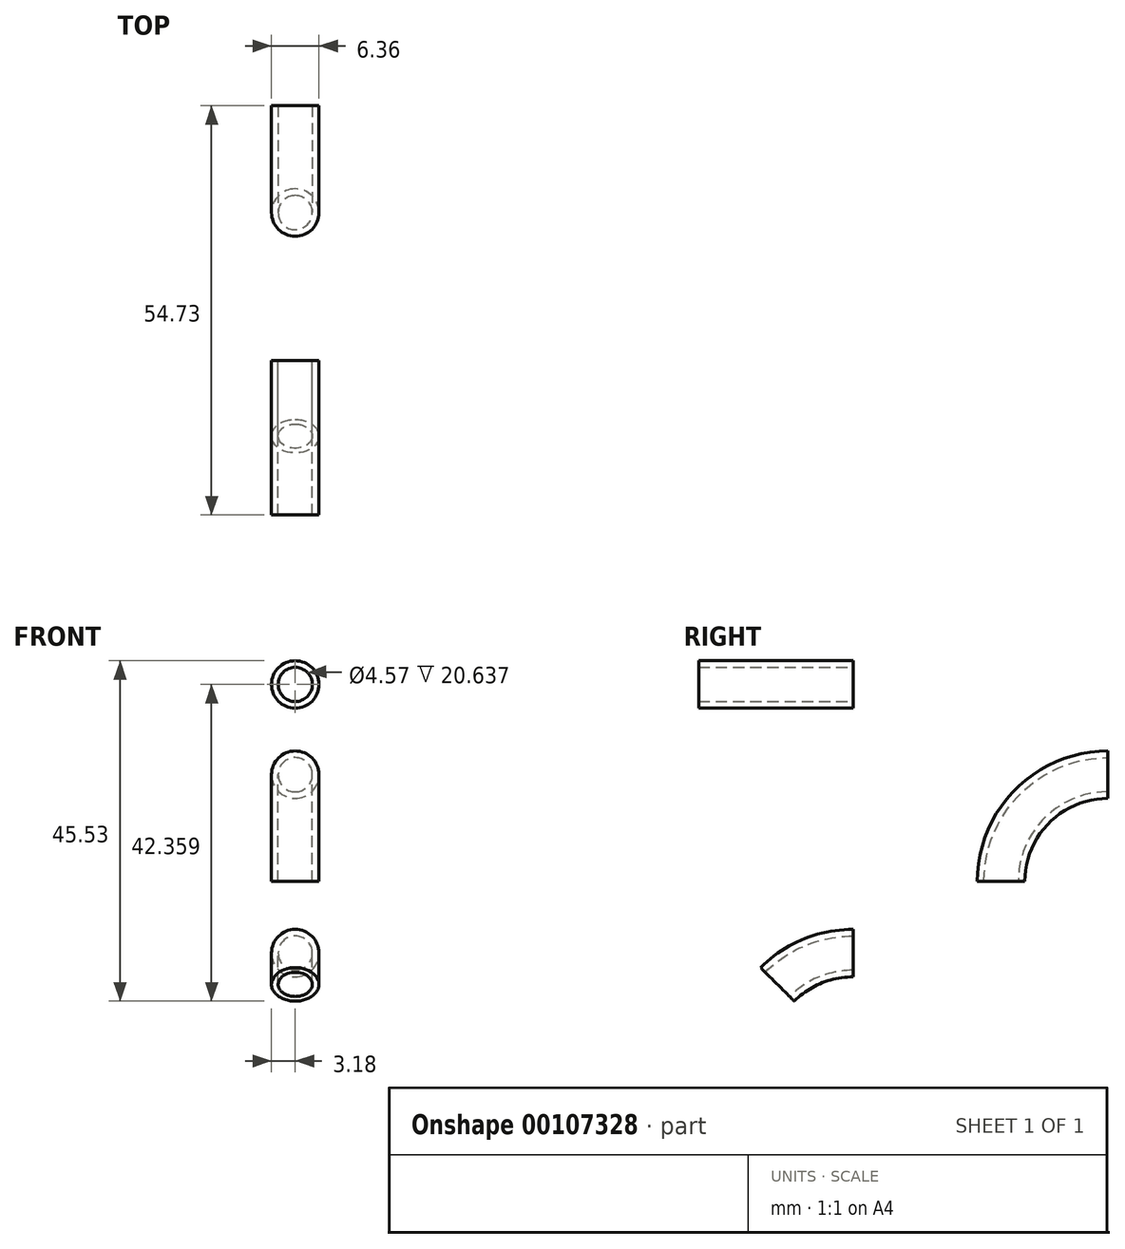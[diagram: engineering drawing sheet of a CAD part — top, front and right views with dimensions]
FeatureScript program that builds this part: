
annotation { "Feature Type Name" : "Feature", "Feature Type Description" : "" }
export const myFeature = defineFeature(function(context is Context, id is Id, definition is map)
    precondition{}
    {
        {
            var Q0;
            Q0=qCreatedBy(makeId("Front.planeOp"),FACE);
            var sketch = newSketch(context, id + "F0", { "sketchPlane" : qUnion([Q0])});
            skCircle(sketch, "E0", {"center": v(0, 0) * mm, "radius": 3.17 * mm});
            skCircle(sketch, "E1", {"center": v(0, 0) * mm, "radius": 2.29 * mm});
            skCircle(sketch, "E2", {"center": v(0, 11.2) * mm, "radius": 3.17 * mm});
            skCircle(sketch, "E3", {"center": v(0, 11.2) * mm, "radius": 2.29 * mm});
            skSolve(sketch);
        }
        {
            var Q0;
            Q0=qCreatedBy(makeId("Right.planeOp"),FACE);
            var sketch = newSketch(context, id + "F1", { "sketchPlane" : qUnion([Q0])});
            skArc(sketch, "E4", {"start": v(0, 0) * mm, "mid": v(-10.1, -4.18) * mm, "end": v(-14.29, -14.29) * mm});
            skSolve(sketch);
        }
        {
            var Q0;
            Q0=makeQuery(id+"F0.imprint","IMPRINT",FACE,{"disambiguationData":[TD([[makeQuery(id+"F0.imprint","IMPRINT",EDGE,{"derivedFrom":sQuery(id+"F0.wireOp",EDGE,"E0")}),1.0]])]});
            var Q1;
            Q1=sQuery(id+"F1.wireOp",EDGE,"E4");
            sweep(context, id + "F2", {"profiles" : qUnion([Q0]), "path" : qUnion([Q1])});
        }
        {
            var Q0;
            Q0=qCreatedBy(makeId("Right.planeOp"),FACE);
            var sketch = newSketch(context, id + "F3", { "sketchPlane" : qUnion([Q0])});
            skArc(sketch, "E5", {"start": v(0, 0) * mm, "mid": v(-5.47, -1.09) * mm, "end": v(-10.1, -4.18) * mm});
            skSolve(sketch);
        }
        {
            var Q0;
            Q0=qCreatedBy(makeId("Front.planeOp"),FACE);
            var sketch = newSketch(context, id + "F4", { "sketchPlane" : qUnion([Q0])});
            skCircle(sketch, "E6", {"center": v(0, 0) * mm, "radius": 3.17 * mm});
            skCircle(sketch, "E7", {"center": v(0, 0) * mm, "radius": 2.29 * mm});
            skSolve(sketch);
        }
        {
            var Q0;
            Q0=makeQuery(id+"F4.imprint","IMPRINT",FACE,{"disambiguationData":[TD([[makeQuery(id+"F4.imprint","IMPRINT",EDGE,{"derivedFrom":sQuery(id+"F4.wireOp",EDGE,"E6")}),1.0]])]});
            var Q1;
            Q1=sQuery(id+"F3.wireOp",EDGE,"E5");
            sweep(context, id + "F5", {"profiles" : qUnion([Q0]), "path" : qUnion([Q1])});
        }
        {
            var Q0;
            Q0=makeQuery(id+"F2.opSweep","SWEPT_BODY",BODY,{"disambiguationData":[OSD([sQuery(id+"F0.wireOp",EDGE,"E0"),sQuery(id+"F0.wireOp",EDGE,"E1"),sQuery(id+"F1.wireOp",EDGE,"E4")])]});
            transform(context, id + "F6", {"entities" : qUnion([Q0]), "transformType" : TransformType.TRANSLATION_3D, "dx" : 0 * mm, "dy" : 34.1 * mm, "dz" : 0 * mm, "makeCopy" : true});
        }
        {
            var Q0;
            Q0=makeQuery(id+"F2.opSweep","SWEPT_BODY",BODY,{"disambiguationData":[OSD([sQuery(id+"F0.wireOp",EDGE,"E0"),sQuery(id+"F0.wireOp",EDGE,"E1"),sQuery(id+"F1.wireOp",EDGE,"E4")])]});
            deleteBodies(context, id + "F7", {"entities" : qUnion([Q0])});
        }
        {
            var Q0;
            Q0=qCreatedBy(makeId("Front.planeOp"),FACE);
            var sketch = newSketch(context, id + "F8", { "sketchPlane" : qUnion([Q0])});
            skCircle(sketch, "E8", {"center": v(0, 12.07) * mm, "radius": 3.17 * mm});
            skCircle(sketch, "E9", {"center": v(0, 12.07) * mm, "radius": 2.29 * mm});
            skSolve(sketch);
        }
        {
            var Q0;
            Q0=makeQuery(id+"F8.imprint","IMPRINT",FACE,{"disambiguationData":[TD([[makeQuery(id+"F8.imprint","IMPRINT",EDGE,{"derivedFrom":sQuery(id+"F8.wireOp",EDGE,"E8")}),1.0]])]});
            extrude(context, id + "F9", {"entities" : qUnion([Q0]), "depth" : 20.64 * mm});
        }
        {
            var Q0;
            Q0=makeQuery(id+"F5.opSweep","SWEPT_BODY",BODY,{"disambiguationData":[OSD([sQuery(id+"F3.wireOp",EDGE,"E5"),sQuery(id+"F4.wireOp",EDGE,"E6"),sQuery(id+"F4.wireOp",EDGE,"E7")])]});
            transform(context, id + "F10", {"entities" : qUnion([Q0]), "transformType" : TransformType.TRANSLATION_3D, "dx" : 0 * mm, "dy" : 0 * mm, "dz" : -23.86 * mm, "makeCopy" : true});
        }
        {
            var Q0;
            Q0=makeQuery(id+"F5.opSweep","SWEPT_BODY",BODY,{"disambiguationData":[OSD([sQuery(id+"F3.wireOp",EDGE,"E5"),sQuery(id+"F4.wireOp",EDGE,"E6"),sQuery(id+"F4.wireOp",EDGE,"E7")])]});
            deleteBodies(context, id + "F11", {"entities" : qUnion([Q0])});
        }
    });
